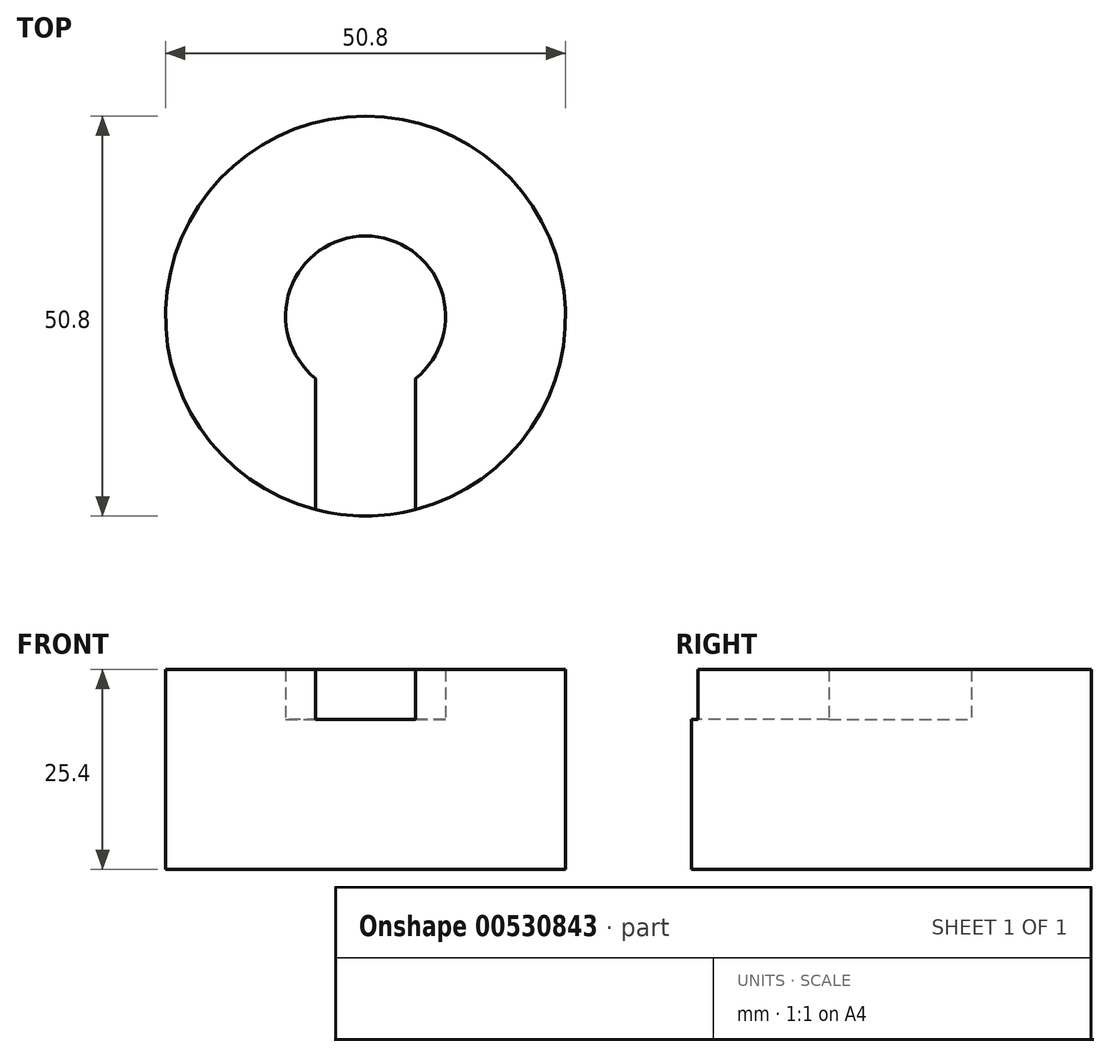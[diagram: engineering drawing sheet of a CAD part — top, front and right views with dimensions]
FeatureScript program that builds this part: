
annotation { "Feature Type Name" : "Feature", "Feature Type Description" : "" }
export const myFeature = defineFeature(function(context is Context, id is Id, definition is map)
    precondition{}
    {
        {
            var Q0;
            Q0=qCreatedBy(makeId("Top.planeOp"),FACE);
            var sketch = newSketch(context, id + "F0", { "sketchPlane" : qUnion([Q0])});
            skCircle(sketch, "E0", {"center": v(0, 0) * mm, "radius": 25.4 * mm});
            skCircle(sketch, "E1", {"center": v(0, 0) * mm, "radius": 10.16 * mm});
            skLineSegment(sketch, "E2", {"start": v(6.35, -7.93) * mm, "end": v(6.35, -24.6) * mm});
            skLineSegment(sketch, "E3", {"start": v(-6.35, -7.93) * mm, "end": v(-6.35, -24.6) * mm});
            skSolve(sketch);
        }
        {
            var Q0;
            Q0=makeQuery(id+"F0.imprint","IMPRINT",FACE,{"disambiguationData":[TD([[makeQuery(id+"F0.imprint","IMPRINT",EDGE,{"derivedFrom":sQuery(id+"F0.wireOp",EDGE,"E1")}),1.0]])]});
            extrude(context, id + "F1", {"entities" : qUnion([Q0]), "depth" : 19.05 * mm, "offsetDistance" : 25.4 * mm});
        }
        {
            var Q0;
            {var subQ0=sQuery(id+"F0.wireOp",EDGE,"E2");Q0=makeQuery(id+"F0.imprint","IMPRINT",FACE,{"disambiguationData":[TD([[makeQuery(id+"F0.imprint","IMPRINT",EDGE,{"derivedFrom":subQ0}),-1.0]])]});}
            extrude(context, id + "F2", {"entities" : qUnion([Q0]), "operationType" : NewBodyOperationType.ADD, "depth" : 19.05 * mm, "offsetDistance" : 25.4 * mm});
        }
        {
            var Q0;
            {var subQ0=sQuery(id+"F0.wireOp",EDGE,"E2");Q0=makeQuery(id+"F0.imprint","IMPRINT",FACE,{"disambiguationData":[TD([[makeQuery(id+"F0.imprint","IMPRINT",EDGE,{"derivedFrom":subQ0}),1.0]])]});}
            extrude(context, id + "F3", {"entities" : qUnion([Q0]), "operationType" : NewBodyOperationType.ADD, "depth" : 25.4 * mm, "offsetDistance" : 25.4 * mm});
        }
    });
